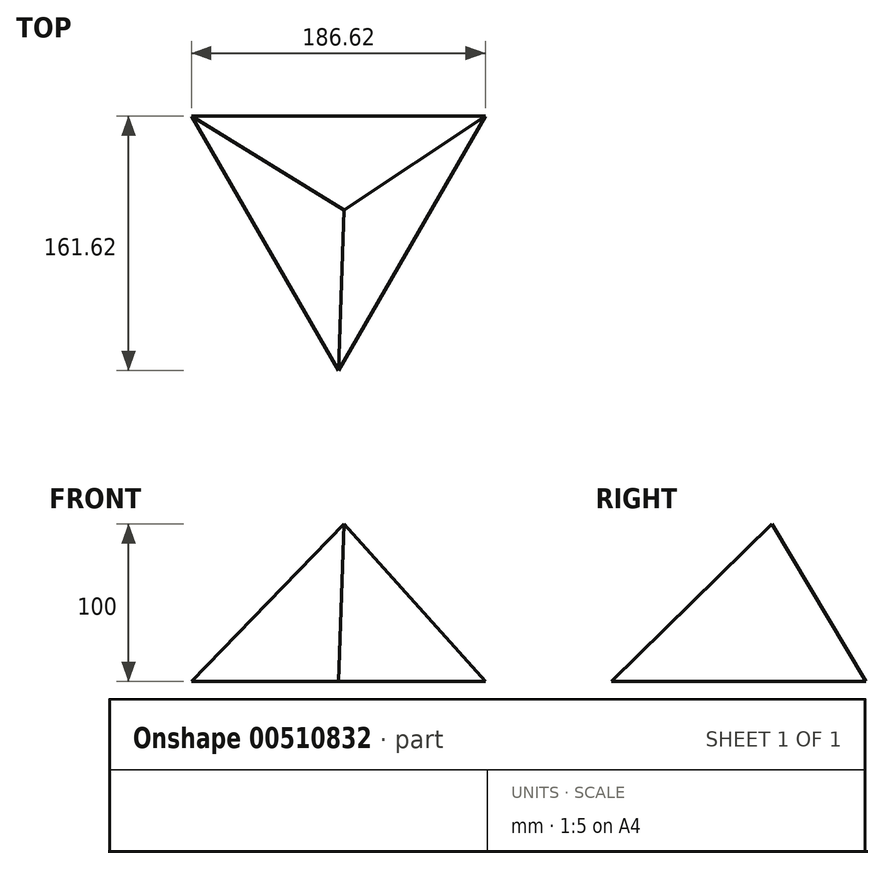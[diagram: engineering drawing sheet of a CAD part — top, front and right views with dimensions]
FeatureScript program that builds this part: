
annotation { "Feature Type Name" : "Feature", "Feature Type Description" : "" }
export const myFeature = defineFeature(function(context is Context, id is Id, definition is map)
    precondition{}
    {
        {
            var Q0;
            Q0=qCreatedBy(makeId("Top.planeOp"),FACE);
            var sketch = newSketch(context, id + "F0", { "sketchPlane" : qUnion([Q0])});
            skCircle(sketch, "E0.cCircle", {"center": v(0, 0) * mm, "radius": 107.75 * mm, "construction": true});
            skLineSegment(sketch, "E0.0", {"start": v(0, -107.75) * mm, "end": v(-93.31, 53.87) * mm});
            skLineSegment(sketch, "E0.1", {"start": v(-93.31, 53.87) * mm, "end": v(93.31, 53.87) * mm});
            skLineSegment(sketch, "E0.2", {"start": v(93.31, 53.87) * mm, "end": v(0, -107.75) * mm});
            skSolve(sketch);
        }
        {
            var Q0;
            Q0=qCreatedBy(makeId("Top.planeOp"),FACE);
            cPlane(context, id + "F1", {"entities" : qUnion([Q0]), "cplaneType" : CPlaneType.OFFSET, "offset" : 100 * mm, "width" : 152.4 * mm, "height" : 152.4 * mm});
        }
        {
            var Q0;
            Q0=qCreatedBy(id+"F1.planeOp",FACE);
            var sketch = newSketch(context, id + "F2", { "sketchPlane" : qUnion([Q0])});
            skPoint(sketch, "E1", {"position": v(3.58, -5.82) * mm});
            skSolve(sketch);
        }
        {
            var Q0;
            Q0=makeQuery(id+"F0.imprint","IMPRINT",FACE,{"disambiguationData":[TD([[makeQuery(id+"F0.imprint","IMPRINT",EDGE,{"derivedFrom":sQuery(id+"F0.wireOp",EDGE,"E0.0")}),-1.0]])]});
            var Q1;
            Q1=sQuery(id+"F2.wireOp",VERTEX,"E1");
            loft(context, id + "F3", {"sheetProfilesArray" : [{ "sheetProfileEntities" : qUnion([Q0]) }, { "sheetProfileEntities" : qUnion([Q1]) }]});
        }
    });
